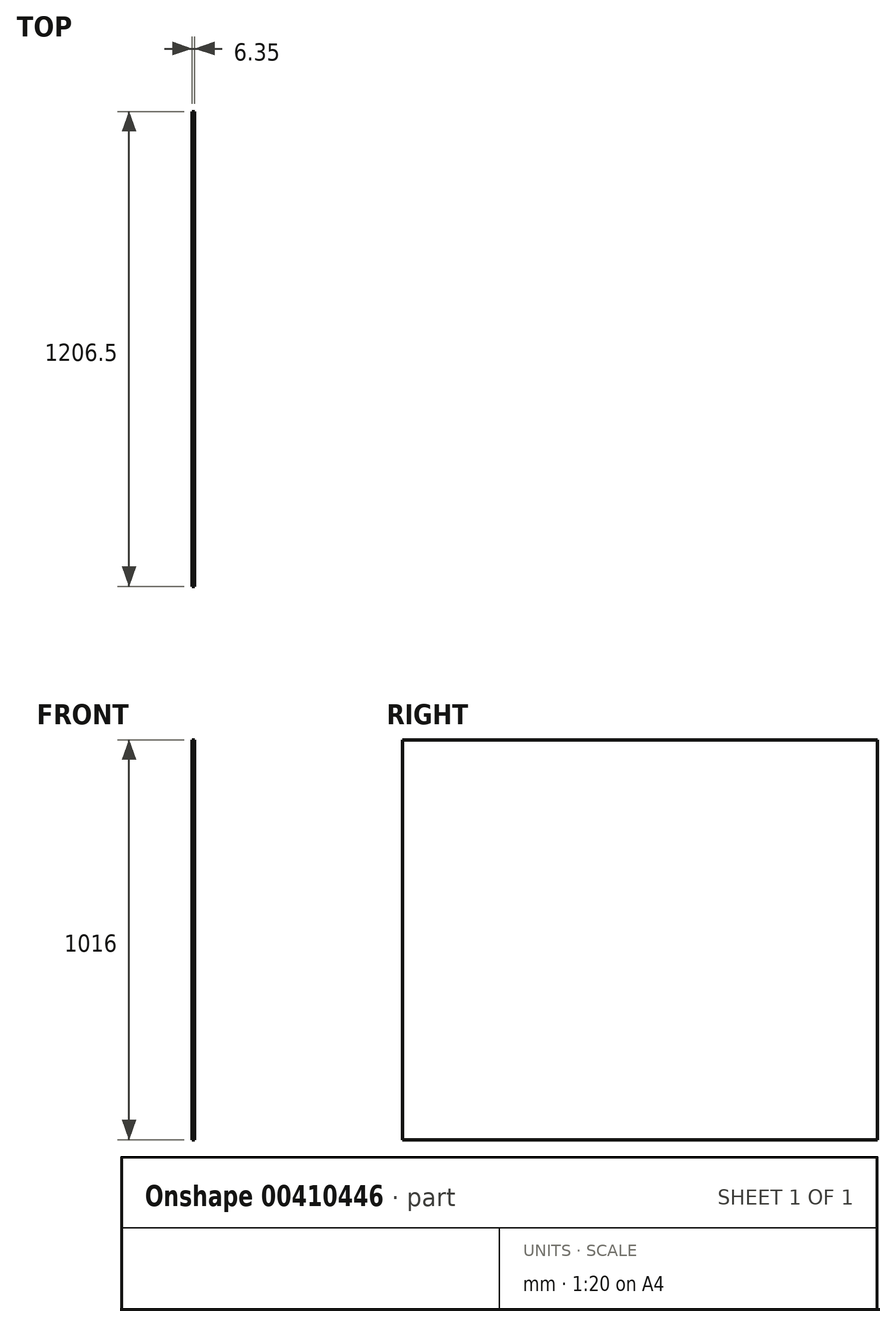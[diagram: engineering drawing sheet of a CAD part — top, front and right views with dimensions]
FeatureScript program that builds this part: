
annotation { "Feature Type Name" : "Feature", "Feature Type Description" : "" }
export const myFeature = defineFeature(function(context is Context, id is Id, definition is map)
    precondition{}
    {
        {
            var Q0;
            Q0=qCreatedBy(makeId("Right.planeOp"),FACE);
            var sketch = newSketch(context, id + "F0", { "sketchPlane" : qUnion([Q0])});
            skLineSegment(sketch, "E0.bottom", {"start": v(-603.25, 508) * mm, "end": v(603.25, 508) * mm});
            skLineSegment(sketch, "E0.top", {"start": v(-603.25, -508) * mm, "end": v(603.25, -508) * mm});
            skLineSegment(sketch, "E0.left", {"start": v(-603.25, 508) * mm, "end": v(-603.25, -508) * mm});
            skLineSegment(sketch, "E0.right", {"start": v(603.25, 508) * mm, "end": v(603.25, -508) * mm});
            skPoint(sketch, "E0.middle", {"position": v(0, 0) * mm});
            skSolve(sketch);
        }
        {
            var Q0;
            Q0 = qSketchRegion(id + "F0", true);
            extrude(context, id + "F1", {"entities" : qUnion([Q0]), "depth" : 6.35 * mm, "offsetDistance" : 25.4 * mm});
        }
    });
